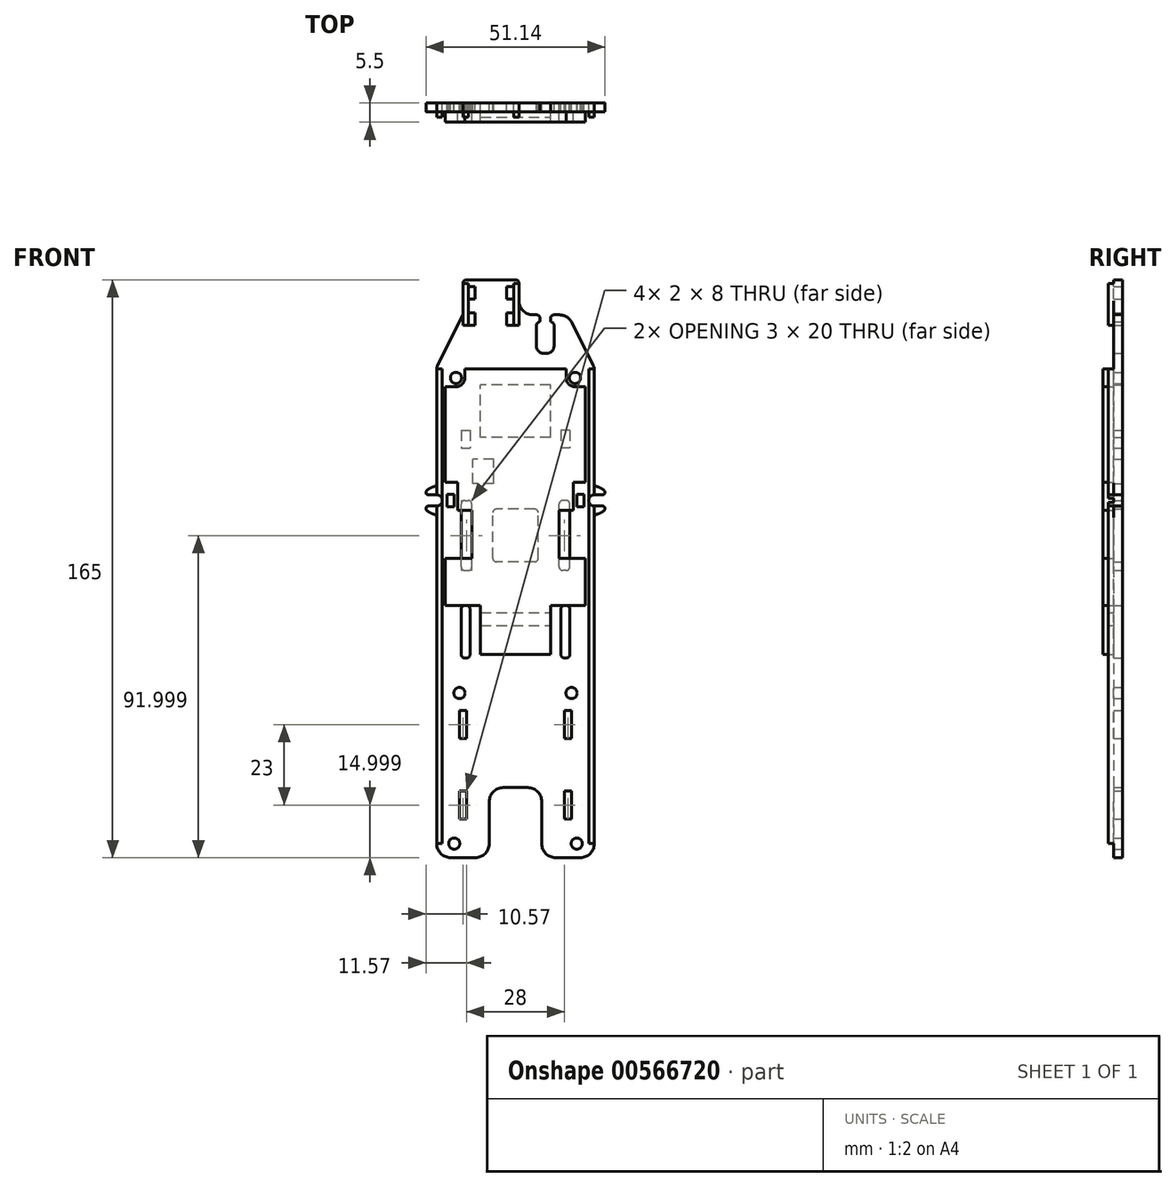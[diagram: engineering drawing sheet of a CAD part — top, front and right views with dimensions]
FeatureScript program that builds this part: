
annotation { "Feature Type Name" : "Feature", "Feature Type Description" : "" }
export const myFeature = defineFeature(function(context is Context, id is Id, definition is map)
    precondition{}
    {
        {
            var Q0;
            Q0=qCreatedBy(makeId("Front.planeOp"),FACE);
            var sketch = newSketch(context, id + "F0", { "sketchPlane" : qUnion([Q0])});
            skPoint(sketch, "E0", {"position": v(-17.5, -62.27) * mm});
            skPoint(sketch, "E1", {"position": v(-16, -19.27) * mm});
            skPoint(sketch, "E2", {"position": v(-17, 70.73) * mm});
            skPoint(sketch, "E3.MirrorP", {"position": v(17, 70.73) * mm});
            skPoint(sketch, "E4.MirrorP", {"position": v(16, -19.27) * mm});
            skPoint(sketch, "E5.MirrorP", {"position": v(17.5, -62.27) * mm});
            skLineSegment(sketch, "E6.bottom", {"start": v(-22.5, 73.73) * mm, "end": v(22.5, 73.73) * mm});
            skLineSegment(sketch, "E6.top", {"start": v(-18.5, -66.27) * mm, "end": v(-11.5, -66.27) * mm});
            skLineSegment(sketch, "E6.left", {"start": v(-22.5, 73.26) * mm, "end": v(-22.5, 40.63) * mm});
            skLineSegment(sketch, "E6.right", {"start": v(22.5, 73.26) * mm, "end": v(22.5, 40.63) * mm});
            skLineSegment(sketch, "E7.top", {"start": v(3.5, -46.27) * mm, "end": v(-3.5, -46.27) * mm});
            skLineSegment(sketch, "E7.left", {"start": v(7.5, -62.27) * mm, "end": v(7.5, -50.27) * mm});
            skLineSegment(sketch, "E7.right", {"start": v(-7.5, -62.27) * mm, "end": v(-7.5, -50.27) * mm});
            skPoint(sketch, "E7.middle", {"position": v(0, -56.27) * mm});
            skPoint(sketch, "E8.visualSharp", {"position": v(-22.5, -66.27) * mm});
            skArc(sketch, "E8.filletArc", {"start": v(-22.5, -62.27) * mm, "mid": v(-21.33, -65.1) * mm, "end": v(-18.5, -66.27) * mm});
            skPoint(sketch, "E9.visualSharp", {"position": v(22.5, -66.27) * mm});
            skArc(sketch, "E9.filletArc", {"start": v(18.5, -66.27) * mm, "mid": v(21.33, -65.1) * mm, "end": v(22.5, -62.27) * mm});
            skPoint(sketch, "E10.visualSharp", {"position": v(-7.5, -46.27) * mm});
            skArc(sketch, "E10.filletArc", {"start": v(-3.5, -46.27) * mm, "mid": v(-6.33, -47.44) * mm, "end": v(-7.5, -50.27) * mm});
            skPoint(sketch, "E11.visualSharp", {"position": v(7.5, -46.27) * mm});
            skArc(sketch, "E11.filletArc", {"start": v(7.5, -50.27) * mm, "mid": v(6.33, -47.44) * mm, "end": v(3.5, -46.27) * mm});
            skLineSegment(sketch, "E12.trimOffspring", {"start": v(11.5, -66.27) * mm, "end": v(18.5, -66.27) * mm});
            skPoint(sketch, "E13.visualSharp", {"position": v(-7.5, -66.27) * mm});
            skArc(sketch, "E13.filletArc", {"start": v(-11.5, -66.27) * mm, "mid": v(-8.67, -65.1) * mm, "end": v(-7.5, -62.27) * mm});
            skPoint(sketch, "E14.visualSharp", {"position": v(7.5, -66.27) * mm});
            skArc(sketch, "E14.filletArc", {"start": v(7.5, -62.27) * mm, "mid": v(8.67, -65.1) * mm, "end": v(11.5, -66.27) * mm});
            skLineSegment(sketch, "E15.bottom", {"start": v(-16, -47.27) * mm, "end": v(-14, -47.27) * mm});
            skLineSegment(sketch, "E15.top", {"start": v(-16, -55.27) * mm, "end": v(-14, -55.27) * mm});
            skLineSegment(sketch, "E15.left", {"start": v(-16, -47.27) * mm, "end": v(-16, -55.27) * mm});
            skLineSegment(sketch, "E15.right", {"start": v(-14, -47.27) * mm, "end": v(-14, -55.27) * mm});
            skLineSegment(sketch, "E16.MirrorCS", {"start": v(16, -47.27) * mm, "end": v(16, -55.27) * mm});
            skLineSegment(sketch, "E17.MirrorCS", {"start": v(14, -47.27) * mm, "end": v(14, -55.27) * mm});
            skLineSegment(sketch, "E18.MirrorCS", {"start": v(16, -47.27) * mm, "end": v(14, -47.27) * mm});
            skLineSegment(sketch, "E19.MirrorCS", {"start": v(16, -55.27) * mm, "end": v(14, -55.27) * mm});
            skLineSegment(sketch, "E20", {"start": v(-22.29, 74.15) * mm, "end": v(-15, 88.73) * mm});
            skLineSegment(sketch, "E21", {"start": v(5, 88.73) * mm, "end": v(6, 88.73) * mm});
            skLineSegment(sketch, "E22", {"start": v(16.1, 86.52) * mm, "end": v(22.29, 74.15) * mm});
            skLineSegment(sketch, "E23.top", {"start": v(-14, 98.73) * mm, "end": v(0, 98.73) * mm});
            skLineSegment(sketch, "E23.left", {"start": v(-15, 88.73) * mm, "end": v(-15, 97.73) * mm});
            skLineSegment(sketch, "E23.right", {"start": v(1, 92.73) * mm, "end": v(1, 97.73) * mm});
            skLineSegment(sketch, "E24.bottom", {"start": v(-13.5, 93.23) * mm, "end": v(-11.5, 93.23) * mm});
            skLineSegment(sketch, "E24.top", {"start": v(-13.5, 96.73) * mm, "end": v(-11.5, 96.73) * mm});
            skLineSegment(sketch, "E24.left", {"start": v(-13.5, 93.23) * mm, "end": v(-13.5, 96.73) * mm});
            skLineSegment(sketch, "E24.right", {"start": v(-11.5, 93.23) * mm, "end": v(-11.5, 96.73) * mm});
            skLineSegment(sketch, "E25", {"start": v(-7, 98.73) * mm, "end": v(-7, 82.75) * mm, "construction": true});
            skLineSegment(sketch, "E26.MirrorCS", {"start": v(-2.5, 93.23) * mm, "end": v(-2.5, 96.73) * mm});
            skLineSegment(sketch, "E27.MirrorCS", {"start": v(-0.5, 96.73) * mm, "end": v(-2.5, 96.73) * mm});
            skLineSegment(sketch, "E28.MirrorCS", {"start": v(-0.5, 93.23) * mm, "end": v(-0.5, 96.73) * mm});
            skLineSegment(sketch, "E29.MirrorCS", {"start": v(-0.5, 93.23) * mm, "end": v(-2.5, 93.23) * mm});
            skLineSegment(sketch, "E30", {"start": v(-15, 91.23) * mm, "end": v(1, 91.23) * mm, "construction": true});
            skLineSegment(sketch, "E31.MirrorCS", {"start": v(-13.5, 85.73) * mm, "end": v(-11.5, 85.73) * mm});
            skLineSegment(sketch, "E32.MirrorCS", {"start": v(-13.5, 89.23) * mm, "end": v(-13.5, 85.73) * mm});
            skLineSegment(sketch, "E33.MirrorCS", {"start": v(-13.5, 89.23) * mm, "end": v(-11.5, 89.23) * mm});
            skLineSegment(sketch, "E34.MirrorCS", {"start": v(-11.5, 89.23) * mm, "end": v(-11.5, 85.73) * mm});
            skLineSegment(sketch, "E35.MirrorCS", {"start": v(-2.5, 89.23) * mm, "end": v(-2.5, 85.73) * mm});
            skLineSegment(sketch, "E36.MirrorCS", {"start": v(-0.5, 85.73) * mm, "end": v(-2.5, 85.73) * mm});
            skLineSegment(sketch, "E37.MirrorCS", {"start": v(-0.5, 89.23) * mm, "end": v(-0.5, 85.73) * mm});
            skLineSegment(sketch, "E38.MirrorCS", {"start": v(-0.5, 89.23) * mm, "end": v(-2.5, 89.23) * mm});
            skPoint(sketch, "E39.visualSharp", {"position": v(1, 88.73) * mm});
            skArc(sketch, "E39.filletArc", {"start": v(1, 92.73) * mm, "mid": v(2.17, 89.9) * mm, "end": v(5, 88.73) * mm});
            skPoint(sketch, "E40.visualSharp", {"position": v(15, 88.73) * mm});
            skArc(sketch, "E40.filletArc", {"start": v(16.1, 86.52) * mm, "mid": v(14.63, 88.13) * mm, "end": v(12.53, 88.73) * mm});
            skPoint(sketch, "E41.visualSharp", {"position": v(1, 98.73) * mm});
            skArc(sketch, "E41.filletArc", {"start": v(1, 97.73) * mm, "mid": v(0.7, 98.44) * mm, "end": v(0, 98.73) * mm});
            skPoint(sketch, "E42.visualSharp", {"position": v(-15, 98.73) * mm});
            skArc(sketch, "E42.filletArc", {"start": v(-14, 98.73) * mm, "mid": v(-14.7, 98.44) * mm, "end": v(-15, 97.73) * mm});
            skPoint(sketch, "E43.visualSharp", {"position": v(22.5, 73.73) * mm});
            skArc(sketch, "E43.filletArc", {"start": v(22.5, 73.26) * mm, "mid": v(22.45, 73.72) * mm, "end": v(22.29, 74.15) * mm});
            skPoint(sketch, "E44.visualSharp", {"position": v(-22.5, 73.73) * mm});
            skArc(sketch, "E44.filletArc", {"start": v(-22.29, 74.15) * mm, "mid": v(-22.45, 73.72) * mm, "end": v(-22.5, 73.26) * mm});
            skLineSegment(sketch, "E45.left", {"start": v(7, 87.73) * mm, "end": v(7, 86.73) * mm});
            skLineSegment(sketch, "E45.right", {"start": v(10, 87.73) * mm, "end": v(10, 86.73) * mm});
            skLineSegment(sketch, "E46.trimOffspring", {"start": v(11, 88.73) * mm, "end": v(12.53, 88.73) * mm});
            skPoint(sketch, "E47.visualSharp", {"position": v(10, 88.73) * mm});
            skArc(sketch, "E47.filletArc", {"start": v(11, 88.73) * mm, "mid": v(10.3, 88.44) * mm, "end": v(10, 87.73) * mm});
            skPoint(sketch, "E48.visualSharp", {"position": v(7, 88.73) * mm});
            skArc(sketch, "E48.filletArc", {"start": v(7, 87.73) * mm, "mid": v(6.7, 88.44) * mm, "end": v(6, 88.73) * mm});
            skPoint(sketch, "E49.visualSharp", {"position": v(7, 76.73) * mm});
            skPoint(sketch, "E50.visualSharp", {"position": v(10, 76.73) * mm});
            skLineSegment(sketch, "E51", {"start": v(-22.5, -39.77) * mm, "end": v(22.5, -39.77) * mm, "construction": true});
            skLineSegment(sketch, "E52.MirrorCS", {"start": v(16, -32.27) * mm, "end": v(16, -24.27) * mm});
            skLineSegment(sketch, "E53.MirrorCS", {"start": v(14, -32.27) * mm, "end": v(14, -24.27) * mm});
            skLineSegment(sketch, "E54.MirrorCS", {"start": v(16, -32.27) * mm, "end": v(14, -32.27) * mm});
            skLineSegment(sketch, "E55.MirrorCS", {"start": v(16, -24.27) * mm, "end": v(14, -24.27) * mm});
            skLineSegment(sketch, "E56.MirrorCS", {"start": v(-14, -32.27) * mm, "end": v(-14, -24.27) * mm});
            skLineSegment(sketch, "E57.MirrorCS", {"start": v(-16, -32.27) * mm, "end": v(-14, -32.27) * mm});
            skLineSegment(sketch, "E58.MirrorCS", {"start": v(-16, -32.27) * mm, "end": v(-16, -24.27) * mm});
            skLineSegment(sketch, "E59.MirrorCS", {"start": v(-16, -24.27) * mm, "end": v(-14, -24.27) * mm});
            skLineSegment(sketch, "E60.bottom", {"start": v(-14.5, -9.27) * mm, "end": v(-14, -9.27) * mm});
            skLineSegment(sketch, "E60.top", {"start": v(-14.5, 5.73) * mm, "end": v(-14, 5.73) * mm});
            skLineSegment(sketch, "E60.left", {"start": v(-15.5, -8.27) * mm, "end": v(-15.5, 4.73) * mm});
            skLineSegment(sketch, "E60.right", {"start": v(-13, -8.27) * mm, "end": v(-13, 4.73) * mm});
            skLineSegment(sketch, "E61.MirrorCS", {"start": v(13, -8.27) * mm, "end": v(13, 4.73) * mm});
            skLineSegment(sketch, "E62.MirrorCS", {"start": v(14.5, 5.73) * mm, "end": v(14, 5.73) * mm});
            skLineSegment(sketch, "E63.MirrorCS", {"start": v(15.5, -8.27) * mm, "end": v(15.5, 4.73) * mm});
            skLineSegment(sketch, "E64.MirrorCS", {"start": v(14.5, -9.27) * mm, "end": v(14, -9.27) * mm});
            skLineSegment(sketch, "E65.bottom", {"start": v(-14.5, 15.73) * mm, "end": v(-13.5, 15.73) * mm});
            skLineSegment(sketch, "E65.top", {"start": v(-14.5, 35.73) * mm, "end": v(-13.5, 35.73) * mm});
            skLineSegment(sketch, "E65.left", {"start": v(-15.5, 16.73) * mm, "end": v(-15.5, 34.73) * mm});
            skLineSegment(sketch, "E65.right", {"start": v(-12.5, 16.73) * mm, "end": v(-12.5, 34.73) * mm});
            skLineSegment(sketch, "E66.MirrorCS", {"start": v(14.5, 15.73) * mm, "end": v(13.5, 15.73) * mm});
            skLineSegment(sketch, "E67.MirrorCS", {"start": v(12.5, 16.73) * mm, "end": v(12.5, 34.73) * mm});
            skLineSegment(sketch, "E68.MirrorCS", {"start": v(14.5, 35.73) * mm, "end": v(13.5, 35.73) * mm});
            skLineSegment(sketch, "E69.MirrorCS", {"start": v(15.5, 16.73) * mm, "end": v(15.5, 34.73) * mm});
            skLineSegment(sketch, "E70.bottom", {"start": v(5.5, 18.23) * mm, "end": v(-5.5, 18.23) * mm});
            skLineSegment(sketch, "E70.top", {"start": v(5.5, 33.23) * mm, "end": v(-5.5, 33.23) * mm});
            skLineSegment(sketch, "E70.left", {"start": v(6.5, 19.23) * mm, "end": v(6.5, 32.23) * mm});
            skLineSegment(sketch, "E70.right", {"start": v(-6.5, 19.23) * mm, "end": v(-6.5, 32.23) * mm});
            skPoint(sketch, "E70.middle", {"position": v(0, 25.73) * mm});
            skPoint(sketch, "E70.middle.positionSnap0", {"position": v(-12.5, 25.73) * mm});
            skPoint(sketch, "E70.centerSnap0", {"position": v(-12.5, 25.73) * mm});
            skPoint(sketch, "E71.visualSharp", {"position": v(-6.5, 33.23) * mm});
            skArc(sketch, "E71.filletArc", {"start": v(-5.5, 33.23) * mm, "mid": v(-6.2, 32.94) * mm, "end": v(-6.5, 32.23) * mm});
            skPoint(sketch, "E72.visualSharp", {"position": v(6.5, 33.23) * mm});
            skArc(sketch, "E72.filletArc", {"start": v(6.5, 32.23) * mm, "mid": v(6.2, 32.94) * mm, "end": v(5.5, 33.23) * mm});
            skPoint(sketch, "E73.visualSharp", {"position": v(6.5, 18.23) * mm});
            skArc(sketch, "E73.filletArc", {"start": v(5.5, 18.23) * mm, "mid": v(6.2, 18.52) * mm, "end": v(6.5, 19.23) * mm});
            skPoint(sketch, "E74.visualSharp", {"position": v(-6.5, 18.23) * mm});
            skArc(sketch, "E74.filletArc", {"start": v(-6.5, 19.23) * mm, "mid": v(-6.2, 18.52) * mm, "end": v(-5.5, 18.23) * mm});
            skPoint(sketch, "E75.visualSharp", {"position": v(-15.5, 15.73) * mm});
            skArc(sketch, "E75.filletArc", {"start": v(-15.5, 16.73) * mm, "mid": v(-15.2, 16.02) * mm, "end": v(-14.5, 15.73) * mm});
            skPoint(sketch, "E76.visualSharp", {"position": v(-15.5, 35.73) * mm});
            skArc(sketch, "E76.filletArc", {"start": v(-14.5, 35.73) * mm, "mid": v(-15.2, 35.44) * mm, "end": v(-15.5, 34.73) * mm});
            skPoint(sketch, "E77.visualSharp", {"position": v(-12.5, 15.73) * mm});
            skArc(sketch, "E77.filletArc", {"start": v(-13.5, 15.73) * mm, "mid": v(-12.8, 16.02) * mm, "end": v(-12.5, 16.73) * mm});
            skPoint(sketch, "E78.visualSharp", {"position": v(-12.5, 35.73) * mm});
            skArc(sketch, "E78.filletArc", {"start": v(-12.5, 34.73) * mm, "mid": v(-12.8, 35.44) * mm, "end": v(-13.5, 35.73) * mm});
            skPoint(sketch, "E79.visualSharp", {"position": v(12.5, 35.73) * mm});
            skArc(sketch, "E79.filletArc", {"start": v(13.5, 35.73) * mm, "mid": v(12.8, 35.44) * mm, "end": v(12.5, 34.73) * mm});
            skPoint(sketch, "E80.visualSharp", {"position": v(15.5, 35.73) * mm});
            skArc(sketch, "E80.filletArc", {"start": v(15.5, 34.73) * mm, "mid": v(15.2, 35.44) * mm, "end": v(14.5, 35.73) * mm});
            skPoint(sketch, "E81.visualSharp", {"position": v(12.5, 15.73) * mm});
            skArc(sketch, "E81.filletArc", {"start": v(12.5, 16.73) * mm, "mid": v(12.8, 16.02) * mm, "end": v(13.5, 15.73) * mm});
            skPoint(sketch, "E82.visualSharp", {"position": v(15.5, 15.73) * mm});
            skArc(sketch, "E82.filletArc", {"start": v(14.5, 15.73) * mm, "mid": v(15.2, 16.02) * mm, "end": v(15.5, 16.73) * mm});
            skPoint(sketch, "E83.visualSharp", {"position": v(13, 5.73) * mm});
            skArc(sketch, "E83.filletArc", {"start": v(14, 5.73) * mm, "mid": v(13.3, 5.44) * mm, "end": v(13, 4.73) * mm});
            skPoint(sketch, "E84.visualSharp", {"position": v(15.5, 5.73) * mm});
            skArc(sketch, "E84.filletArc", {"start": v(15.5, 4.73) * mm, "mid": v(15.2, 5.44) * mm, "end": v(14.5, 5.73) * mm});
            skPoint(sketch, "E85.visualSharp", {"position": v(13, -9.27) * mm});
            skArc(sketch, "E85.filletArc", {"start": v(13, -8.27) * mm, "mid": v(13.3, -8.98) * mm, "end": v(14, -9.27) * mm});
            skPoint(sketch, "E86.visualSharp", {"position": v(15.5, -9.27) * mm});
            skArc(sketch, "E86.filletArc", {"start": v(14.5, -9.27) * mm, "mid": v(15.2, -8.98) * mm, "end": v(15.5, -8.27) * mm});
            skPoint(sketch, "E87.visualSharp", {"position": v(-15.5, -9.27) * mm});
            skArc(sketch, "E87.filletArc", {"start": v(-15.5, -8.27) * mm, "mid": v(-15.2, -8.98) * mm, "end": v(-14.5, -9.27) * mm});
            skPoint(sketch, "E88.visualSharp", {"position": v(-15.5, 5.73) * mm});
            skArc(sketch, "E88.filletArc", {"start": v(-14.5, 5.73) * mm, "mid": v(-15.2, 5.44) * mm, "end": v(-15.5, 4.73) * mm});
            skPoint(sketch, "E89.visualSharp", {"position": v(-13, 5.73) * mm});
            skArc(sketch, "E89.filletArc", {"start": v(-13, 4.73) * mm, "mid": v(-13.3, 5.44) * mm, "end": v(-14, 5.73) * mm});
            skPoint(sketch, "E90.visualSharp", {"position": v(-13, -9.27) * mm});
            skArc(sketch, "E90.filletArc", {"start": v(-14, -9.27) * mm, "mid": v(-13.3, -8.98) * mm, "end": v(-13, -8.27) * mm});
            skLineSegment(sketch, "E91.bottom", {"start": v(-15.5, 55.73) * mm, "end": v(-13, 55.73) * mm});
            skLineSegment(sketch, "E91.top", {"start": v(-15.5, 50.73) * mm, "end": v(-13, 50.73) * mm});
            skLineSegment(sketch, "E91.left", {"start": v(-15.5, 55.73) * mm, "end": v(-15.5, 50.73) * mm});
            skLineSegment(sketch, "E91.right", {"start": v(-13, 55.73) * mm, "end": v(-13, 50.73) * mm});
            skLineSegment(sketch, "E92.MirrorCS", {"start": v(15.5, 50.73) * mm, "end": v(13, 50.73) * mm});
            skLineSegment(sketch, "E93.MirrorCS", {"start": v(15.5, 55.73) * mm, "end": v(13, 55.73) * mm});
            skLineSegment(sketch, "E94.MirrorCS", {"start": v(13, 55.73) * mm, "end": v(13, 50.73) * mm});
            skLineSegment(sketch, "E95.MirrorCS", {"start": v(15.5, 55.73) * mm, "end": v(15.5, 50.73) * mm});
            skLineSegment(sketch, "E96.bottom", {"start": v(10, 53.73) * mm, "end": v(-10, 53.73) * mm});
            skLineSegment(sketch, "E96.top", {"start": v(10, 68.73) * mm, "end": v(-10, 68.73) * mm});
            skLineSegment(sketch, "E96.left", {"start": v(10, 53.73) * mm, "end": v(10, 68.73) * mm});
            skLineSegment(sketch, "E96.right", {"start": v(-10, 53.73) * mm, "end": v(-10, 68.73) * mm});
            skPoint(sketch, "E96.middle", {"position": v(0, 61.23) * mm});
            skLineSegment(sketch, "E97.bottom", {"start": v(-6.17, 40.53) * mm, "end": v(-12.17, 40.53) * mm});
            skLineSegment(sketch, "E97.top", {"start": v(-6.17, 47.53) * mm, "end": v(-12.17, 47.53) * mm});
            skLineSegment(sketch, "E97.left", {"start": v(-6.17, 40.53) * mm, "end": v(-6.17, 47.53) * mm});
            skLineSegment(sketch, "E97.right", {"start": v(-12.17, 40.53) * mm, "end": v(-12.17, 47.53) * mm});
            skPoint(sketch, "E97.middle", {"position": v(-9.17, 44.03) * mm});
            skLineSegment(sketch, "E98.bottom", {"start": v(9, 77.73) * mm, "end": v(8, 77.73) * mm});
            skLineSegment(sketch, "E98.top", {"start": v(10, 86.73) * mm, "end": v(10, 86.73) * mm});
            skLineSegment(sketch, "E98.left", {"start": v(11, 79.73) * mm, "end": v(11, 85.73) * mm});
            skLineSegment(sketch, "E98.right", {"start": v(6, 79.73) * mm, "end": v(6, 85.73) * mm});
            skPoint(sketch, "E98.middle", {"position": v(8.5, 82.23) * mm});
            skPoint(sketch, "E98.middle.positionSnap0", {"position": v(8.5, 76.73) * mm});
            skPoint(sketch, "E98.centerSnap0", {"position": v(8.5, 76.73) * mm});
            skPoint(sketch, "E99.orphan", {"position": v(8, 76.73) * mm});
            skPoint(sketch, "E45.top.end.orphan", {"position": v(9, 76.73) * mm});
            skLineSegment(sketch, "E100.trimOffspring", {"start": v(7, 86.73) * mm, "end": v(7, 86.73) * mm});
            skPoint(sketch, "E101.visualSharp", {"position": v(6, 77.73) * mm});
            skArc(sketch, "E101.filletArc", {"start": v(6, 79.73) * mm, "mid": v(6.59, 78.31) * mm, "end": v(8, 77.73) * mm});
            skPoint(sketch, "E102.visualSharp", {"position": v(11, 77.73) * mm});
            skArc(sketch, "E102.filletArc", {"start": v(9, 77.73) * mm, "mid": v(10.41, 78.31) * mm, "end": v(11, 79.73) * mm});
            skPoint(sketch, "E103.visualSharp", {"position": v(6, 86.73) * mm});
            skArc(sketch, "E103.filletArc", {"start": v(7, 86.73) * mm, "mid": v(6.3, 86.44) * mm, "end": v(6, 85.73) * mm});
            skPoint(sketch, "E104.visualSharp", {"position": v(11, 86.73) * mm});
            skArc(sketch, "E104.filletArc", {"start": v(11, 85.73) * mm, "mid": v(10.7, 86.44) * mm, "end": v(10, 86.73) * mm});
            skArc(sketch, "E105", {"start": v(-23.3, 39.65) * mm, "mid": v(-24.42, 39.24) * mm, "end": v(-25.37, 38.52) * mm});
            skArc(sketch, "E106", {"start": v(-22.5, 34.13) * mm, "mid": v(-20.9, 35.73) * mm, "end": v(-22.5, 37.33) * mm});
            skLineSegment(sketch, "E107", {"start": v(-22.5, 37.33) * mm, "end": v(-24.87, 37.33) * mm});
            skLineSegment(sketch, "E108", {"start": v(-22.5, 34.13) * mm, "end": v(-24.87, 34.13) * mm});
            skArc(sketch, "E109.trimOffspring", {"start": v(-25.37, 32.94) * mm, "mid": v(-24.42, 32.22) * mm, "end": v(-23.3, 31.8) * mm});
            skPoint(sketch, "E110.visualSharp", {"position": v(-26.17, 37.33) * mm});
            skArc(sketch, "E110.filletArc", {"start": v(-25.37, 38.52) * mm, "mid": v(-25.51, 37.76) * mm, "end": v(-24.87, 37.33) * mm});
            skPoint(sketch, "E111.visualSharp", {"position": v(-26.17, 34.13) * mm});
            skArc(sketch, "E111.filletArc", {"start": v(-24.87, 34.13) * mm, "mid": v(-25.51, 33.7) * mm, "end": v(-25.37, 32.94) * mm});
            skLineSegment(sketch, "E112.trimOffspring", {"start": v(-22.5, 30.83) * mm, "end": v(-22.5, -62.27) * mm});
            skPoint(sketch, "E113.visualSharp", {"position": v(-22.5, 39.73) * mm});
            skArc(sketch, "E113.filletArc", {"start": v(-23.3, 39.65) * mm, "mid": v(-22.73, 40) * mm, "end": v(-22.5, 40.63) * mm});
            skPoint(sketch, "E114.visualSharp", {"position": v(-22.5, 31.73) * mm});
            skArc(sketch, "E114.filletArc", {"start": v(-22.5, 30.83) * mm, "mid": v(-22.73, 31.46) * mm, "end": v(-23.3, 31.8) * mm});
            skLineSegment(sketch, "E115.bottom", {"start": v(-19.5, 37.48) * mm, "end": v(-17.5, 37.48) * mm});
            skLineSegment(sketch, "E115.top", {"start": v(-19.5, 33.98) * mm, "end": v(-17.5, 33.98) * mm});
            skLineSegment(sketch, "E115.left", {"start": v(-19.5, 37.48) * mm, "end": v(-19.5, 33.98) * mm});
            skLineSegment(sketch, "E115.right", {"start": v(-17.5, 37.48) * mm, "end": v(-17.5, 33.98) * mm});
            skPoint(sketch, "E115.middle", {"position": v(-18.5, 35.73) * mm});
            skLineSegment(sketch, "E116.MirrorCS", {"start": v(19.5, 37.48) * mm, "end": v(17.5, 37.48) * mm});
            skLineSegment(sketch, "E117.MirrorCS", {"start": v(17.5, 37.48) * mm, "end": v(17.5, 33.98) * mm});
            skLineSegment(sketch, "E118.MirrorCS", {"start": v(19.5, 33.98) * mm, "end": v(17.5, 33.98) * mm});
            skLineSegment(sketch, "E119.MirrorCS", {"start": v(19.5, 37.48) * mm, "end": v(19.5, 33.98) * mm});
            skArc(sketch, "E120.MirrorCS", {"start": v(25.37, 32.94) * mm, "mid": v(24.42, 32.22) * mm, "end": v(23.3, 31.8) * mm});
            skPoint(sketch, "E121.MirrorP", {"position": v(22.5, 31.73) * mm});
            skPoint(sketch, "E122.MirrorP", {"position": v(26.17, 34.13) * mm});
            skArc(sketch, "E123.MirrorCS", {"start": v(24.87, 34.13) * mm, "mid": v(25.51, 33.7) * mm, "end": v(25.37, 32.94) * mm});
            skPoint(sketch, "E124.MirrorP", {"position": v(26.17, 37.33) * mm});
            skArc(sketch, "E125.MirrorCS", {"start": v(25.37, 38.52) * mm, "mid": v(25.51, 37.76) * mm, "end": v(24.87, 37.33) * mm});
            skPoint(sketch, "E126.MirrorP", {"position": v(22.5, 39.73) * mm});
            skArc(sketch, "E127.MirrorCS", {"start": v(23.3, 39.65) * mm, "mid": v(24.42, 39.24) * mm, "end": v(25.37, 38.52) * mm});
            skArc(sketch, "E128.MirrorCS", {"start": v(22.5, 34.13) * mm, "mid": v(20.9, 35.73) * mm, "end": v(22.5, 37.33) * mm});
            skLineSegment(sketch, "E129.MirrorCS", {"start": v(22.5, 37.33) * mm, "end": v(24.87, 37.33) * mm});
            skLineSegment(sketch, "E130.MirrorCS", {"start": v(22.5, 34.13) * mm, "end": v(24.87, 34.13) * mm});
            skArc(sketch, "E131.MirrorCS", {"start": v(23.3, 39.65) * mm, "mid": v(22.73, 40) * mm, "end": v(22.5, 40.63) * mm});
            skArc(sketch, "E132.MirrorCS", {"start": v(22.5, 30.83) * mm, "mid": v(22.73, 31.46) * mm, "end": v(23.3, 31.8) * mm});
            skLineSegment(sketch, "E133.trimOffspring", {"start": v(22.5, 30.83) * mm, "end": v(22.5, -62.27) * mm});
            skSolve(sketch);
        }
        {
            var Q0;
            Q0=makeQuery(id+"F0.imprint","IMPRINT",FACE,{"disambiguationData":[TD([[makeQuery(id+"F0.imprint","IMPRINT",EDGE,{"derivedFrom":sQuery(id+"F0.wireOp",EDGE,"E6.top")}),1.0]])]});
            var Q1;
            {var subQ1=sQuery(id+"F0.wireOp",EDGE,"E20");Q1=makeQuery(id+"F0.imprint","IMPRINT",FACE,{"disambiguationData":[TD([[makeQuery(id+"F0.imprint","IMPRINT",EDGE,{"derivedFrom":subQ1}),-1.0]])]});}
            extrude(context, id + "F1", {"entities" : qUnion([Q0, Q1]), "depth" : 2.5 * mm, "offsetDistance" : 25 * mm});
        }
        {
            var Q0;
            Q0=sQuery(id+"F0.wireOp",VERTEX,"E2");
            var Q1;
            Q1=sQuery(id+"F0.wireOp",VERTEX,"E3.MirrorP");
            var Q2;
            Q2=sQuery(id+"F0.wireOp",VERTEX,"E1");
            var Q3;
            Q3=sQuery(id+"F0.wireOp",VERTEX,"E4.MirrorP");
            var Q4;
            Q4=sQuery(id+"F0.wireOp",VERTEX,"E0");
            var Q5;
            Q5=sQuery(id+"F0.wireOp",VERTEX,"E5.MirrorP");
            var Q6;
            Q6=makeQuery(id+"F1.opExtrude","SWEPT_BODY",BODY,{"disambiguationData":[OSD([sQuery(id+"F0.wireOp",EDGE,"E6.top"),sQuery(id+"F0.wireOp",EDGE,"E6.left"),sQuery(id+"F0.wireOp",EDGE,"E6.right"),sQuery(id+"F0.wireOp",EDGE,"E7.top"),sQuery(id+"F0.wireOp",EDGE,"E7.left"),sQuery(id+"F0.wireOp",EDGE,"E7.right"),sQuery(id+"F0.wireOp",EDGE,"E8.filletArc"),sQuery(id+"F0.wireOp",EDGE,"E9.filletArc"),sQuery(id+"F0.wireOp",EDGE,"E10.filletArc"),sQuery(id+"F0.wireOp",EDGE,"E11.filletArc"),sQuery(id+"F0.wireOp",EDGE,"E12.trimOffspring"),sQuery(id+"F0.wireOp",EDGE,"E13.filletArc"),sQuery(id+"F0.wireOp",EDGE,"E14.filletArc"),sQuery(id+"F0.wireOp",EDGE,"E15.bottom"),sQuery(id+"F0.wireOp",EDGE,"E15.top"),sQuery(id+"F0.wireOp",EDGE,"E15.left"),sQuery(id+"F0.wireOp",EDGE,"E15.right"),sQuery(id+"F0.wireOp",EDGE,"E16.MirrorCS"),sQuery(id+"F0.wireOp",EDGE,"E17.MirrorCS"),sQuery(id+"F0.wireOp",EDGE,"E18.MirrorCS"),sQuery(id+"F0.wireOp",EDGE,"E19.MirrorCS"),sQuery(id+"F0.wireOp",EDGE,"E20"),sQuery(id+"F0.wireOp",EDGE,"E21"),sQuery(id+"F0.wireOp",EDGE,"E22"),sQuery(id+"F0.wireOp",EDGE,"E23.top"),sQuery(id+"F0.wireOp",EDGE,"E23.left"),sQuery(id+"F0.wireOp",EDGE,"E23.right"),sQuery(id+"F0.wireOp",EDGE,"E24.bottom"),sQuery(id+"F0.wireOp",EDGE,"E24.top"),sQuery(id+"F0.wireOp",EDGE,"E24.left"),sQuery(id+"F0.wireOp",EDGE,"E24.right"),sQuery(id+"F0.wireOp",EDGE,"E26.MirrorCS"),sQuery(id+"F0.wireOp",EDGE,"E27.MirrorCS"),sQuery(id+"F0.wireOp",EDGE,"E28.MirrorCS"),sQuery(id+"F0.wireOp",EDGE,"E29.MirrorCS"),sQuery(id+"F0.wireOp",EDGE,"E31.MirrorCS"),sQuery(id+"F0.wireOp",EDGE,"E32.MirrorCS"),sQuery(id+"F0.wireOp",EDGE,"E33.MirrorCS"),sQuery(id+"F0.wireOp",EDGE,"E34.MirrorCS"),sQuery(id+"F0.wireOp",EDGE,"E35.MirrorCS"),sQuery(id+"F0.wireOp",EDGE,"E36.MirrorCS"),sQuery(id+"F0.wireOp",EDGE,"E37.MirrorCS"),sQuery(id+"F0.wireOp",EDGE,"E38.MirrorCS"),sQuery(id+"F0.wireOp",EDGE,"E39.filletArc"),sQuery(id+"F0.wireOp",EDGE,"E40.filletArc"),sQuery(id+"F0.wireOp",EDGE,"E41.filletArc"),sQuery(id+"F0.wireOp",EDGE,"E42.filletArc"),sQuery(id+"F0.wireOp",EDGE,"E43.filletArc"),sQuery(id+"F0.wireOp",EDGE,"E44.filletArc"),sQuery(id+"F0.wireOp",EDGE,"E45.top"),sQuery(id+"F0.wireOp",EDGE,"E45.left"),sQuery(id+"F0.wireOp",EDGE,"E45.right"),sQuery(id+"F0.wireOp",EDGE,"E46.trimOffspring"),sQuery(id+"F0.wireOp",EDGE,"E47.filletArc"),sQuery(id+"F0.wireOp",EDGE,"E48.filletArc"),sQuery(id+"F0.wireOp",EDGE,"E49.filletArc"),sQuery(id+"F0.wireOp",EDGE,"E50.filletArc"),sQuery(id+"F0.wireOp",EDGE,"E52.MirrorCS"),sQuery(id+"F0.wireOp",EDGE,"E53.MirrorCS"),sQuery(id+"F0.wireOp",EDGE,"E54.MirrorCS"),sQuery(id+"F0.wireOp",EDGE,"E55.MirrorCS"),sQuery(id+"F0.wireOp",EDGE,"E56.MirrorCS"),sQuery(id+"F0.wireOp",EDGE,"E57.MirrorCS"),sQuery(id+"F0.wireOp",EDGE,"E58.MirrorCS"),sQuery(id+"F0.wireOp",EDGE,"E59.MirrorCS"),sQuery(id+"F0.wireOp",EDGE,"E60.bottom"),sQuery(id+"F0.wireOp",EDGE,"E60.top"),sQuery(id+"F0.wireOp",EDGE,"E60.left"),sQuery(id+"F0.wireOp",EDGE,"E60.right"),sQuery(id+"F0.wireOp",EDGE,"E61.MirrorCS"),sQuery(id+"F0.wireOp",EDGE,"E62.MirrorCS"),sQuery(id+"F0.wireOp",EDGE,"E63.MirrorCS"),sQuery(id+"F0.wireOp",EDGE,"E64.MirrorCS"),sQuery(id+"F0.wireOp",EDGE,"E65.bottom"),sQuery(id+"F0.wireOp",EDGE,"E65.top"),sQuery(id+"F0.wireOp",EDGE,"E65.left"),sQuery(id+"F0.wireOp",EDGE,"E65.right"),sQuery(id+"F0.wireOp",EDGE,"E66.MirrorCS"),sQuery(id+"F0.wireOp",EDGE,"E67.MirrorCS"),sQuery(id+"F0.wireOp",EDGE,"E68.MirrorCS"),sQuery(id+"F0.wireOp",EDGE,"E69.MirrorCS"),sQuery(id+"F0.wireOp",EDGE,"E70.bottom"),sQuery(id+"F0.wireOp",EDGE,"E70.top"),sQuery(id+"F0.wireOp",EDGE,"E70.left"),sQuery(id+"F0.wireOp",EDGE,"E70.right"),sQuery(id+"F0.wireOp",EDGE,"E71.filletArc"),sQuery(id+"F0.wireOp",EDGE,"E72.filletArc"),sQuery(id+"F0.wireOp",EDGE,"E73.filletArc"),sQuery(id+"F0.wireOp",EDGE,"E74.filletArc"),sQuery(id+"F0.wireOp",EDGE,"E75.filletArc"),sQuery(id+"F0.wireOp",EDGE,"E76.filletArc"),sQuery(id+"F0.wireOp",EDGE,"E77.filletArc"),sQuery(id+"F0.wireOp",EDGE,"E78.filletArc"),sQuery(id+"F0.wireOp",EDGE,"E79.filletArc"),sQuery(id+"F0.wireOp",EDGE,"E80.filletArc"),sQuery(id+"F0.wireOp",EDGE,"E81.filletArc"),sQuery(id+"F0.wireOp",EDGE,"E82.filletArc"),sQuery(id+"F0.wireOp",EDGE,"E83.filletArc"),sQuery(id+"F0.wireOp",EDGE,"E84.filletArc"),sQuery(id+"F0.wireOp",EDGE,"E85.filletArc"),sQuery(id+"F0.wireOp",EDGE,"E86.filletArc"),sQuery(id+"F0.wireOp",EDGE,"E87.filletArc"),sQuery(id+"F0.wireOp",EDGE,"E88.filletArc"),sQuery(id+"F0.wireOp",EDGE,"E89.filletArc"),sQuery(id+"F0.wireOp",EDGE,"E90.filletArc"),sQuery(id+"F0.wireOp",EDGE,"E91.bottom"),sQuery(id+"F0.wireOp",EDGE,"E91.top"),sQuery(id+"F0.wireOp",EDGE,"E91.left"),sQuery(id+"F0.wireOp",EDGE,"E91.right"),sQuery(id+"F0.wireOp",EDGE,"E92.MirrorCS"),sQuery(id+"F0.wireOp",EDGE,"E93.MirrorCS"),sQuery(id+"F0.wireOp",EDGE,"E94.MirrorCS"),sQuery(id+"F0.wireOp",EDGE,"E95.MirrorCS"),sQuery(id+"F0.wireOp",EDGE,"E96.bottom"),sQuery(id+"F0.wireOp",EDGE,"E96.top"),sQuery(id+"F0.wireOp",EDGE,"E96.left"),sQuery(id+"F0.wireOp",EDGE,"E96.right"),sQuery(id+"F0.wireOp",EDGE,"E97.bottom"),sQuery(id+"F0.wireOp",EDGE,"E97.top"),sQuery(id+"F0.wireOp",EDGE,"E97.left"),sQuery(id+"F0.wireOp",EDGE,"E97.right")])]});
            hole(context, id + "F2", {"style" : HoleStyle.SIMPLE, "endStyle" : HoleEndStyle.THROUGH, "oppositeDirection" : true, "holeDiameter" : 3.2 * mm, "isTappedThrough" : true, "tappedDepth" : 12 * mm, "tapClearance" : 3, "locations" : qUnion([Q0, Q1, Q2, Q3, Q4, Q5]), "scope" : qUnion([Q6])});
        }
        {
            var Q0;
            Q0=makeQuery(id+"F1.opExtrude","CAP_FACE",FACE,{"disambiguationData":[OSD([sQuery(id+"F0.wireOp",EDGE,"E6.top"),sQuery(id+"F0.wireOp",EDGE,"E6.left"),sQuery(id+"F0.wireOp",EDGE,"E6.right"),sQuery(id+"F0.wireOp",EDGE,"E7.top"),sQuery(id+"F0.wireOp",EDGE,"E7.left"),sQuery(id+"F0.wireOp",EDGE,"E7.right"),sQuery(id+"F0.wireOp",EDGE,"E8.filletArc"),sQuery(id+"F0.wireOp",EDGE,"E9.filletArc"),sQuery(id+"F0.wireOp",EDGE,"E10.filletArc"),sQuery(id+"F0.wireOp",EDGE,"E11.filletArc"),sQuery(id+"F0.wireOp",EDGE,"E12.trimOffspring"),sQuery(id+"F0.wireOp",EDGE,"E13.filletArc"),sQuery(id+"F0.wireOp",EDGE,"E14.filletArc"),sQuery(id+"F0.wireOp",EDGE,"E15.bottom"),sQuery(id+"F0.wireOp",EDGE,"E15.top"),sQuery(id+"F0.wireOp",EDGE,"E15.left"),sQuery(id+"F0.wireOp",EDGE,"E15.right"),sQuery(id+"F0.wireOp",EDGE,"E16.MirrorCS"),sQuery(id+"F0.wireOp",EDGE,"E17.MirrorCS"),sQuery(id+"F0.wireOp",EDGE,"E18.MirrorCS"),sQuery(id+"F0.wireOp",EDGE,"E19.MirrorCS"),sQuery(id+"F0.wireOp",EDGE,"E20"),sQuery(id+"F0.wireOp",EDGE,"E21"),sQuery(id+"F0.wireOp",EDGE,"E22"),sQuery(id+"F0.wireOp",EDGE,"E23.top"),sQuery(id+"F0.wireOp",EDGE,"E23.left"),sQuery(id+"F0.wireOp",EDGE,"E23.right"),sQuery(id+"F0.wireOp",EDGE,"E24.bottom"),sQuery(id+"F0.wireOp",EDGE,"E24.top"),sQuery(id+"F0.wireOp",EDGE,"E24.left"),sQuery(id+"F0.wireOp",EDGE,"E24.right"),sQuery(id+"F0.wireOp",EDGE,"E26.MirrorCS"),sQuery(id+"F0.wireOp",EDGE,"E27.MirrorCS"),sQuery(id+"F0.wireOp",EDGE,"E28.MirrorCS"),sQuery(id+"F0.wireOp",EDGE,"E29.MirrorCS"),sQuery(id+"F0.wireOp",EDGE,"E31.MirrorCS"),sQuery(id+"F0.wireOp",EDGE,"E32.MirrorCS"),sQuery(id+"F0.wireOp",EDGE,"E33.MirrorCS"),sQuery(id+"F0.wireOp",EDGE,"E34.MirrorCS"),sQuery(id+"F0.wireOp",EDGE,"E35.MirrorCS"),sQuery(id+"F0.wireOp",EDGE,"E36.MirrorCS"),sQuery(id+"F0.wireOp",EDGE,"E37.MirrorCS"),sQuery(id+"F0.wireOp",EDGE,"E38.MirrorCS"),sQuery(id+"F0.wireOp",EDGE,"E39.filletArc"),sQuery(id+"F0.wireOp",EDGE,"E40.filletArc"),sQuery(id+"F0.wireOp",EDGE,"E41.filletArc"),sQuery(id+"F0.wireOp",EDGE,"E42.filletArc"),sQuery(id+"F0.wireOp",EDGE,"E43.filletArc"),sQuery(id+"F0.wireOp",EDGE,"E44.filletArc"),sQuery(id+"F0.wireOp",EDGE,"E45.top"),sQuery(id+"F0.wireOp",EDGE,"E45.left"),sQuery(id+"F0.wireOp",EDGE,"E45.right"),sQuery(id+"F0.wireOp",EDGE,"E46.trimOffspring"),sQuery(id+"F0.wireOp",EDGE,"E47.filletArc"),sQuery(id+"F0.wireOp",EDGE,"E48.filletArc"),sQuery(id+"F0.wireOp",EDGE,"E49.filletArc"),sQuery(id+"F0.wireOp",EDGE,"E50.filletArc"),sQuery(id+"F0.wireOp",EDGE,"E52.MirrorCS"),sQuery(id+"F0.wireOp",EDGE,"E53.MirrorCS"),sQuery(id+"F0.wireOp",EDGE,"E54.MirrorCS"),sQuery(id+"F0.wireOp",EDGE,"E55.MirrorCS"),sQuery(id+"F0.wireOp",EDGE,"E56.MirrorCS"),sQuery(id+"F0.wireOp",EDGE,"E57.MirrorCS"),sQuery(id+"F0.wireOp",EDGE,"E58.MirrorCS"),sQuery(id+"F0.wireOp",EDGE,"E59.MirrorCS"),sQuery(id+"F0.wireOp",EDGE,"E60.bottom"),sQuery(id+"F0.wireOp",EDGE,"E60.top"),sQuery(id+"F0.wireOp",EDGE,"E60.left"),sQuery(id+"F0.wireOp",EDGE,"E60.right"),sQuery(id+"F0.wireOp",EDGE,"E61.MirrorCS"),sQuery(id+"F0.wireOp",EDGE,"E62.MirrorCS"),sQuery(id+"F0.wireOp",EDGE,"E63.MirrorCS"),sQuery(id+"F0.wireOp",EDGE,"E64.MirrorCS"),sQuery(id+"F0.wireOp",EDGE,"E65.bottom"),sQuery(id+"F0.wireOp",EDGE,"E65.top"),sQuery(id+"F0.wireOp",EDGE,"E65.left"),sQuery(id+"F0.wireOp",EDGE,"E65.right"),sQuery(id+"F0.wireOp",EDGE,"E66.MirrorCS"),sQuery(id+"F0.wireOp",EDGE,"E67.MirrorCS"),sQuery(id+"F0.wireOp",EDGE,"E68.MirrorCS"),sQuery(id+"F0.wireOp",EDGE,"E69.MirrorCS"),sQuery(id+"F0.wireOp",EDGE,"E70.bottom"),sQuery(id+"F0.wireOp",EDGE,"E70.top"),sQuery(id+"F0.wireOp",EDGE,"E70.left"),sQuery(id+"F0.wireOp",EDGE,"E70.right"),sQuery(id+"F0.wireOp",EDGE,"E71.filletArc"),sQuery(id+"F0.wireOp",EDGE,"E72.filletArc"),sQuery(id+"F0.wireOp",EDGE,"E73.filletArc"),sQuery(id+"F0.wireOp",EDGE,"E74.filletArc"),sQuery(id+"F0.wireOp",EDGE,"E75.filletArc"),sQuery(id+"F0.wireOp",EDGE,"E76.filletArc"),sQuery(id+"F0.wireOp",EDGE,"E77.filletArc"),sQuery(id+"F0.wireOp",EDGE,"E78.filletArc"),sQuery(id+"F0.wireOp",EDGE,"E79.filletArc"),sQuery(id+"F0.wireOp",EDGE,"E80.filletArc"),sQuery(id+"F0.wireOp",EDGE,"E81.filletArc"),sQuery(id+"F0.wireOp",EDGE,"E82.filletArc"),sQuery(id+"F0.wireOp",EDGE,"E83.filletArc"),sQuery(id+"F0.wireOp",EDGE,"E84.filletArc"),sQuery(id+"F0.wireOp",EDGE,"E85.filletArc"),sQuery(id+"F0.wireOp",EDGE,"E86.filletArc"),sQuery(id+"F0.wireOp",EDGE,"E87.filletArc"),sQuery(id+"F0.wireOp",EDGE,"E88.filletArc"),sQuery(id+"F0.wireOp",EDGE,"E89.filletArc"),sQuery(id+"F0.wireOp",EDGE,"E90.filletArc"),sQuery(id+"F0.wireOp",EDGE,"E91.bottom"),sQuery(id+"F0.wireOp",EDGE,"E91.top"),sQuery(id+"F0.wireOp",EDGE,"E91.left"),sQuery(id+"F0.wireOp",EDGE,"E91.right"),sQuery(id+"F0.wireOp",EDGE,"E92.MirrorCS"),sQuery(id+"F0.wireOp",EDGE,"E93.MirrorCS"),sQuery(id+"F0.wireOp",EDGE,"E94.MirrorCS"),sQuery(id+"F0.wireOp",EDGE,"E95.MirrorCS"),sQuery(id+"F0.wireOp",EDGE,"E96.bottom"),sQuery(id+"F0.wireOp",EDGE,"E96.top"),sQuery(id+"F0.wireOp",EDGE,"E96.left"),sQuery(id+"F0.wireOp",EDGE,"E96.right"),sQuery(id+"F0.wireOp",EDGE,"E97.bottom"),sQuery(id+"F0.wireOp",EDGE,"E97.top"),sQuery(id+"F0.wireOp",EDGE,"E97.left"),sQuery(id+"F0.wireOp",EDGE,"E97.right")])],"isStart":false});
            var sketch = newSketch(context, id + "F3", { "sketchPlane" : qUnion([Q0])});
            skLineSegment(sketch, "E134.bottom", {"start": v(-22.5, 73.26) * mm, "end": v(-21, 73.26) * mm});
            skLineSegment(sketch, "E134.top", {"start": v(-22.5, -62.27) * mm, "end": v(-21, -62.27) * mm});
            skLineSegment(sketch, "E134.left", {"start": v(-22.5, 73.26) * mm, "end": v(-22.5, -62.27) * mm});
            skLineSegment(sketch, "E134.right", {"start": v(-21, 73.26) * mm, "end": v(-21, -62.27) * mm});
            skLineSegment(sketch, "E135.MirrorCS", {"start": v(22.5, 73.26) * mm, "end": v(21, 73.26) * mm});
            skLineSegment(sketch, "E136.MirrorCS", {"start": v(22.5, -62.27) * mm, "end": v(21, -62.27) * mm});
            skLineSegment(sketch, "E137.MirrorCS", {"start": v(21, 73.26) * mm, "end": v(21, -62.27) * mm});
            skLineSegment(sketch, "E138.MirrorCS", {"start": v(22.5, 73.26) * mm, "end": v(22.5, -62.27) * mm});
            skLineSegment(sketch, "E139.bottom", {"start": v(-15, 97.73) * mm, "end": v(-13.5, 97.73) * mm});
            skLineSegment(sketch, "E139.top", {"start": v(-15, 85.73) * mm, "end": v(-13.5, 85.73) * mm});
            skLineSegment(sketch, "E139.left", {"start": v(-15, 97.73) * mm, "end": v(-15, 85.73) * mm});
            skLineSegment(sketch, "E139.right", {"start": v(-13.5, 97.73) * mm, "end": v(-13.5, 85.73) * mm});
            skLineSegment(sketch, "E140.bottom", {"start": v(-0.5, 97.73) * mm, "end": v(1, 97.73) * mm});
            skLineSegment(sketch, "E140.top", {"start": v(-0.5, 85.73) * mm, "end": v(1, 85.73) * mm});
            skLineSegment(sketch, "E140.left", {"start": v(-0.5, 97.73) * mm, "end": v(-0.5, 85.73) * mm});
            skLineSegment(sketch, "E140.right", {"start": v(1, 97.73) * mm, "end": v(1, 85.73) * mm});
            skSolve(sketch);
        }
        {
            var Q0;
            Q0 = qSketchRegion(id + "F3", true);
            extrude(context, id + "F4", {"entities" : qUnion([Q0]), "operationType" : NewBodyOperationType.ADD, "depth" : 1.5 * mm, "offsetDistance" : 25 * mm});
        }
        {
            var Q0;
            Q0=makeQuery(id+"F4.opExtrude","CAP_FACE",FACE,{"disambiguationData":[OSD([sQuery(id+"F3.wireOp",EDGE,"E135.MirrorCS"),sQuery(id+"F3.wireOp",EDGE,"E136.MirrorCS"),sQuery(id+"F3.wireOp",EDGE,"E137.MirrorCS"),sQuery(id+"F3.wireOp",EDGE,"E138.MirrorCS")])],"isStart":true});
            var sketch = newSketch(context, id + "F5", { "sketchPlane" : qUnion([Q0])});
            skLineSegment(sketch, "E141.0.0", {"start": v(-22.5, 37.33) * mm, "end": v(-22.5, 34.13) * mm});
            skArc(sketch, "E141.0.1", {"start": v(-22.5, 34.13) * mm, "mid": v(-21.59, 34.42) * mm, "end": v(-21, 35.17) * mm});
            skLineSegment(sketch, "E141.0.2", {"start": v(-21, 35.17) * mm, "end": v(-21, 36.29) * mm});
            skArc(sketch, "E141.0.3", {"start": v(-21, 36.29) * mm, "mid": v(-21.59, 37.04) * mm, "end": v(-22.5, 37.33) * mm});
            skArc(sketch, "E142.0.0", {"start": v(21, 35.17) * mm, "mid": v(21.59, 34.42) * mm, "end": v(22.5, 34.13) * mm});
            skLineSegment(sketch, "E142.0.1", {"start": v(22.5, 34.13) * mm, "end": v(22.5, 37.33) * mm});
            skArc(sketch, "E142.0.2", {"start": v(22.5, 37.33) * mm, "mid": v(21.59, 37.04) * mm, "end": v(21, 36.29) * mm});
            skLineSegment(sketch, "E142.0.3", {"start": v(21, 36.29) * mm, "end": v(21, 35.17) * mm});
            skSolve(sketch);
        }
        {
            var Q0;
            Q0 = qSketchRegion(id + "F5", true);
            extrude(context, id + "F6", {"entities" : qUnion([Q0]), "operationType" : NewBodyOperationType.REMOVE, "oppositeDirection" : true, "depth" : 25 * mm, "offsetDistance" : 25 * mm});
        }
        {
            var Q0;
            {var subQ0=sQuery(id+"F0.wireOp",EDGE,"E83.filletArc");var subQ1=sQuery(id+"F0.wireOp",EDGE,"E82.filletArc");var subQ2=sQuery(id+"F0.wireOp",EDGE,"E81.filletArc");var subQ3=sQuery(id+"F0.wireOp",EDGE,"E80.filletArc");var subQ4=sQuery(id+"F0.wireOp",EDGE,"E79.filletArc");var subQ5=sQuery(id+"F0.wireOp",EDGE,"E78.filletArc");var subQ6=sQuery(id+"F0.wireOp",EDGE,"E77.filletArc");var subQ7=sQuery(id+"F0.wireOp",EDGE,"E76.filletArc");var subQ8=sQuery(id+"F0.wireOp",EDGE,"E75.filletArc");var subQ9=sQuery(id+"F0.wireOp",EDGE,"E74.filletArc");var subQ10=sQuery(id+"F0.wireOp",EDGE,"E73.filletArc");var subQ11=sQuery(id+"F0.wireOp",EDGE,"E72.filletArc");var subQ12=sQuery(id+"F0.wireOp",EDGE,"E71.filletArc");var subQ13=sQuery(id+"F0.wireOp",EDGE,"E70.right");var subQ14=sQuery(id+"F0.wireOp",EDGE,"E70.left");var subQ15=sQuery(id+"F0.wireOp",EDGE,"E70.top");var subQ16=sQuery(id+"F0.wireOp",EDGE,"E70.bottom");var subQ17=sQuery(id+"F0.wireOp",EDGE,"E69.MirrorCS");var subQ18=sQuery(id+"F0.wireOp",EDGE,"E68.MirrorCS");var subQ19=sQuery(id+"F0.wireOp",EDGE,"E67.MirrorCS");var subQ20=sQuery(id+"F0.wireOp",EDGE,"E66.MirrorCS");var subQ21=sQuery(id+"F0.wireOp",EDGE,"E65.right");var subQ22=sQuery(id+"F0.wireOp",EDGE,"E65.left");var subQ23=sQuery(id+"F0.wireOp",EDGE,"E65.top");var subQ24=sQuery(id+"F0.wireOp",EDGE,"E65.bottom");var subQ25=sQuery(id+"F0.wireOp",EDGE,"E64.MirrorCS");var subQ26=sQuery(id+"F0.wireOp",EDGE,"E63.MirrorCS");var subQ27=sQuery(id+"F0.wireOp",EDGE,"E62.MirrorCS");var subQ28=sQuery(id+"F0.wireOp",EDGE,"E61.MirrorCS");var subQ29=sQuery(id+"F0.wireOp",EDGE,"E60.right");var subQ30=sQuery(id+"F0.wireOp",EDGE,"E60.left");var subQ31=sQuery(id+"F0.wireOp",EDGE,"E60.top");var subQ32=sQuery(id+"F0.wireOp",EDGE,"E60.bottom");var subQ33=sQuery(id+"F0.wireOp",EDGE,"E59.MirrorCS");var subQ34=sQuery(id+"F0.wireOp",EDGE,"E58.MirrorCS");var subQ35=sQuery(id+"F0.wireOp",EDGE,"E57.MirrorCS");var subQ36=sQuery(id+"F0.wireOp",EDGE,"E56.MirrorCS");var subQ37=sQuery(id+"F0.wireOp",EDGE,"E55.MirrorCS");var subQ38=sQuery(id+"F0.wireOp",EDGE,"E54.MirrorCS");var subQ39=sQuery(id+"F0.wireOp",EDGE,"E53.MirrorCS");var subQ40=sQuery(id+"F0.wireOp",EDGE,"E52.MirrorCS");var subQ41=sQuery(id+"F0.wireOp",EDGE,"E48.filletArc");var subQ42=sQuery(id+"F0.wireOp",EDGE,"E47.filletArc");var subQ43=sQuery(id+"F0.wireOp",EDGE,"E46.trimOffspring");var subQ44=sQuery(id+"F0.wireOp",EDGE,"E45.right");var subQ45=sQuery(id+"F0.wireOp",EDGE,"E45.left");var subQ46=sQuery(id+"F0.wireOp",EDGE,"E44.filletArc");var subQ47=sQuery(id+"F0.wireOp",EDGE,"E43.filletArc");var subQ48=sQuery(id+"F0.wireOp",EDGE,"E42.filletArc");var subQ49=sQuery(id+"F0.wireOp",EDGE,"E19.MirrorCS");var subQ50=sQuery(id+"F0.wireOp",EDGE,"E18.MirrorCS");var subQ51=sQuery(id+"F0.wireOp",EDGE,"E17.MirrorCS");var subQ52=sQuery(id+"F0.wireOp",EDGE,"E16.MirrorCS");var subQ53=sQuery(id+"F0.wireOp",EDGE,"E15.right");var subQ54=sQuery(id+"F0.wireOp",EDGE,"E15.left");var subQ55=sQuery(id+"F0.wireOp",EDGE,"E15.top");var subQ56=sQuery(id+"F0.wireOp",EDGE,"E15.bottom");var subQ57=sQuery(id+"F0.wireOp",EDGE,"E14.filletArc");var subQ58=sQuery(id+"F0.wireOp",EDGE,"E13.filletArc");var subQ59=sQuery(id+"F0.wireOp",EDGE,"E12.trimOffspring");var subQ60=sQuery(id+"F0.wireOp",EDGE,"E6.right");var subQ61=sQuery(id+"F0.wireOp",EDGE,"E6.left");var subQ62=sQuery(id+"F0.wireOp",EDGE,"E7.top");var subQ63=sQuery(id+"F0.wireOp",EDGE,"E20");var subQ64=sQuery(id+"F0.wireOp",EDGE,"E84.filletArc");var subQ65=sQuery(id+"F0.wireOp",EDGE,"E6.top");var subQ66=sQuery(id+"F0.wireOp",EDGE,"E41.filletArc");var subQ67=sQuery(id+"F0.wireOp",EDGE,"E11.filletArc");var subQ68=sQuery(id+"F0.wireOp",EDGE,"E7.left");var subQ69=sQuery(id+"F0.wireOp",EDGE,"E7.right");var subQ70=sQuery(id+"F0.wireOp",EDGE,"E8.filletArc");var subQ71=sQuery(id+"F0.wireOp",EDGE,"E9.filletArc");var subQ72=sQuery(id+"F0.wireOp",EDGE,"E10.filletArc");var subQ73=sQuery(id+"F0.wireOp",EDGE,"E21");var subQ74=sQuery(id+"F0.wireOp",EDGE,"E22");var subQ75=sQuery(id+"F0.wireOp",EDGE,"E23.top");var subQ76=sQuery(id+"F0.wireOp",EDGE,"E23.left");var subQ77=sQuery(id+"F0.wireOp",EDGE,"E23.right");var subQ78=sQuery(id+"F0.wireOp",EDGE,"E24.bottom");var subQ79=sQuery(id+"F0.wireOp",EDGE,"E24.top");var subQ80=sQuery(id+"F0.wireOp",EDGE,"E24.left");var subQ81=sQuery(id+"F0.wireOp",EDGE,"E24.right");var subQ82=sQuery(id+"F0.wireOp",EDGE,"E26.MirrorCS");var subQ83=sQuery(id+"F0.wireOp",EDGE,"E27.MirrorCS");var subQ84=sQuery(id+"F0.wireOp",EDGE,"E28.MirrorCS");var subQ85=sQuery(id+"F0.wireOp",EDGE,"E29.MirrorCS");var subQ86=sQuery(id+"F0.wireOp",EDGE,"E31.MirrorCS");var subQ87=sQuery(id+"F0.wireOp",EDGE,"E32.MirrorCS");var subQ88=sQuery(id+"F0.wireOp",EDGE,"E33.MirrorCS");var subQ89=sQuery(id+"F0.wireOp",EDGE,"E34.MirrorCS");var subQ90=sQuery(id+"F0.wireOp",EDGE,"E35.MirrorCS");var subQ91=sQuery(id+"F0.wireOp",EDGE,"E36.MirrorCS");var subQ92=sQuery(id+"F0.wireOp",EDGE,"E37.MirrorCS");var subQ93=sQuery(id+"F0.wireOp",EDGE,"E38.MirrorCS");var subQ94=sQuery(id+"F0.wireOp",EDGE,"E39.filletArc");var subQ95=sQuery(id+"F0.wireOp",EDGE,"E40.filletArc");var subQ96=sQuery(id+"F0.wireOp",EDGE,"E85.filletArc");var subQ98=sQuery(id+"F0.wireOp",EDGE,"E86.filletArc");var subQ102=sQuery(id+"F0.wireOp",EDGE,"E87.filletArc");var subQ103=sQuery(id+"F0.wireOp",EDGE,"E88.filletArc");var subQ104=sQuery(id+"F0.wireOp",EDGE,"E89.filletArc");var subQ106=sQuery(id+"F0.wireOp",EDGE,"E114.filletArc");var subQ108=sQuery(id+"F0.wireOp",EDGE,"E108");var subQ109=sQuery(id+"F0.wireOp",EDGE,"E106");var subQ112=sQuery(id+"F0.wireOp",EDGE,"E107");var subQ114=sQuery(id+"F0.wireOp",EDGE,"E113.filletArc");var subQ116=sQuery(id+"F0.wireOp",EDGE,"E90.filletArc");var subQ117=sQuery(id+"F0.wireOp",EDGE,"E91.bottom");var subQ118=sQuery(id+"F0.wireOp",EDGE,"E91.top");var subQ120=sQuery(id+"F0.wireOp",EDGE,"E91.left");var subQ124=sQuery(id+"F0.wireOp",EDGE,"E91.right");var subQ125=sQuery(id+"F0.wireOp",EDGE,"E92.MirrorCS");var subQ126=sQuery(id+"F0.wireOp",EDGE,"E93.MirrorCS");var subQ127=sQuery(id+"F0.wireOp",EDGE,"E94.MirrorCS");var subQ129=sQuery(id+"F0.wireOp",EDGE,"E132.MirrorCS");var subQ131=sQuery(id+"F0.wireOp",EDGE,"E130.MirrorCS");var subQ132=sQuery(id+"F0.wireOp",EDGE,"E128.MirrorCS");var subQ135=sQuery(id+"F0.wireOp",EDGE,"E129.MirrorCS");var subQ137=sQuery(id+"F0.wireOp",EDGE,"E131.MirrorCS");var subQ139=sQuery(id+"F0.wireOp",EDGE,"E95.MirrorCS");var subQ140=sQuery(id+"F0.wireOp",EDGE,"E96.bottom");var subQ141=sQuery(id+"F0.wireOp",EDGE,"E96.top");var subQ142=sQuery(id+"F0.wireOp",EDGE,"E96.left");var subQ143=sQuery(id+"F0.wireOp",EDGE,"E96.right");var subQ144=sQuery(id+"F0.wireOp",EDGE,"E97.bottom");var subQ145=sQuery(id+"F0.wireOp",EDGE,"E97.top");var subQ146=sQuery(id+"F0.wireOp",EDGE,"E97.left");var subQ147=sQuery(id+"F0.wireOp",EDGE,"E97.right");var subQ148=sQuery(id+"F0.wireOp",EDGE,"E98.bottom");var subQ149=sQuery(id+"F0.wireOp",EDGE,"E98.left");var subQ150=sQuery(id+"F0.wireOp",EDGE,"E98.right");var subQ151=sQuery(id+"F0.wireOp",EDGE,"E101.filletArc");var subQ152=sQuery(id+"F0.wireOp",EDGE,"E102.filletArc");var subQ153=sQuery(id+"F0.wireOp",EDGE,"E103.filletArc");var subQ154=sQuery(id+"F0.wireOp",EDGE,"E104.filletArc");var subQ155=sQuery(id+"F0.wireOp",EDGE,"E112.trimOffspring");var subQ156=sQuery(id+"F0.wireOp",EDGE,"E115.bottom");var subQ157=sQuery(id+"F0.wireOp",EDGE,"E115.top");var subQ158=sQuery(id+"F0.wireOp",EDGE,"E115.left");var subQ159=sQuery(id+"F0.wireOp",EDGE,"E115.right");var subQ160=sQuery(id+"F0.wireOp",EDGE,"E116.MirrorCS");var subQ161=sQuery(id+"F0.wireOp",EDGE,"E117.MirrorCS");var subQ162=sQuery(id+"F0.wireOp",EDGE,"E118.MirrorCS");var subQ163=sQuery(id+"F0.wireOp",EDGE,"E119.MirrorCS");var subQ164=sQuery(id+"F0.wireOp",EDGE,"E133.trimOffspring");Q0=makeQuery(id+"F4.boolean.opBoolean","SPLIT",FACE,{"disambiguationData":[TD([makeQuery(id+"F1.opExtrude","SWEPT_FACE",FACE,{"disambiguationData":[OSD([subQ65])]})])],"derivedFrom":makeQuery(id+"F1.opExtrude","CAP_FACE",FACE,{"disambiguationData":[OSD([subQ65,subQ61,subQ60,subQ62,subQ68,subQ69,subQ70,subQ71,subQ72,subQ67,subQ59,subQ58,subQ57,subQ56,subQ55,subQ54,subQ53,subQ52,subQ51,subQ50,subQ49,subQ63,subQ73,subQ74,subQ75,subQ76,subQ77,subQ78,subQ79,subQ80,subQ81,subQ82,subQ83,subQ84,subQ85,subQ86,subQ87,subQ88,subQ89,subQ90,subQ91,subQ92,subQ93,subQ94,subQ95,subQ66,subQ48,subQ47,subQ46,subQ45,subQ44,subQ43,subQ42,subQ41,subQ40,subQ39,subQ38,subQ37,subQ36,subQ35,subQ34,subQ33,subQ32,subQ31,subQ30,subQ29,subQ28,subQ27,subQ26,subQ25,subQ24,subQ23,subQ22,subQ21,subQ20,subQ19,subQ18,subQ17,subQ16,subQ15,subQ14,subQ13,subQ12,subQ11,subQ10,subQ9,subQ8,subQ7,subQ6,subQ5,subQ4,subQ3,subQ2,subQ1,subQ0,subQ64,subQ96,subQ98,subQ102,subQ103,subQ104,subQ116,subQ117,subQ118,subQ120,subQ124,subQ125,subQ126,subQ127,subQ139,subQ140,subQ141,subQ142,subQ143,subQ144,subQ145,subQ146,subQ147,subQ148,subQ149,subQ150,subQ151,subQ152,subQ153,subQ154,sQuery(id+"F0.wireOp",EDGE,"E105"),subQ109,subQ112,subQ108,sQuery(id+"F0.wireOp",EDGE,"E109.trimOffspring"),sQuery(id+"F0.wireOp",EDGE,"E110.filletArc"),sQuery(id+"F0.wireOp",EDGE,"E111.filletArc"),subQ155,subQ114,subQ106,subQ156,subQ157,subQ158,subQ159,subQ160,subQ161,subQ162,subQ163,sQuery(id+"F0.wireOp",EDGE,"E120.MirrorCS"),sQuery(id+"F0.wireOp",EDGE,"E123.MirrorCS"),sQuery(id+"F0.wireOp",EDGE,"E125.MirrorCS"),sQuery(id+"F0.wireOp",EDGE,"E127.MirrorCS"),subQ132,subQ135,subQ131,subQ137,subQ129,subQ164])],"isStart":false})});}
            var sketch = newSketch(context, id + "F7", { "sketchPlane" : qUnion([Q0])});
            skCircle(sketch, "E143.0", {"center": v(-17, 70.73) * mm, "radius": 1.6 * mm, "construction": true});
            skCircle(sketch, "E144.0", {"center": v(17, 70.73) * mm, "radius": 1.6 * mm, "construction": true});
            skLineSegment(sketch, "E145", {"start": v(0, 5.73) * mm, "end": v(20, 5.73) * mm});
            skLineSegment(sketch, "E146", {"start": v(21, 5.73) * mm, "end": v(21, 33.98) * mm});
            skLineSegment(sketch, "E147", {"start": v(20, 19.23) * mm, "end": v(12.5, 19.23) * mm});
            skLineSegment(sketch, "E148", {"start": v(12.5, 19.23) * mm, "end": v(12.5, 32.93) * mm});
            skLineSegment(sketch, "E149", {"start": v(12.5, 32.93) * mm, "end": v(16.5, 32.93) * mm});
            skLineSegment(sketch, "E150", {"start": v(16.5, 40.96) * mm, "end": v(20, 40.96) * mm});
            skLineSegment(sketch, "E151", {"start": v(21, 40.96) * mm, "end": v(21, 73.26) * mm});
            skLineSegment(sketch, "E152", {"start": v(14.47, 73.26) * mm, "end": v(0, 73.26) * mm});
            skLineSegment(sketch, "E153", {"start": v(0, 0) * mm, "end": v(0, 0) * mm});
            skLineSegment(sketch, "E154.0", {"start": v(20, 5.73) * mm, "end": v(20, 19.23) * mm});
            skLineSegment(sketch, "E155.0", {"start": v(16.5, 32.93) * mm, "end": v(16.5, 40.96) * mm});
            skPoint(sketch, "E156.start.orphan", {"position": v(17.5, 32.93) * mm});
            skLineSegment(sketch, "E157.0", {"start": v(20, 40.96) * mm, "end": v(20, 68.2) * mm});
            skPoint(sketch, "E158.orphan", {"position": v(21, 19.23) * mm});
            skLineSegment(sketch, "E159.MirrorCS", {"start": v(-14.47, 73.26) * mm, "end": v(0, 73.26) * mm});
            skLineSegment(sketch, "E160.MirrorCS", {"start": v(-20, 40.96) * mm, "end": v(-20, 68.2) * mm});
            skLineSegment(sketch, "E161.MirrorCS", {"start": v(-16.5, 40.96) * mm, "end": v(-20, 40.96) * mm});
            skLineSegment(sketch, "E162.MirrorCS", {"start": v(-16.5, 32.93) * mm, "end": v(-16.5, 40.96) * mm});
            skLineSegment(sketch, "E163.MirrorCS", {"start": v(-12.5, 32.93) * mm, "end": v(-16.5, 32.93) * mm});
            skLineSegment(sketch, "E164.MirrorCS", {"start": v(-12.5, 19.23) * mm, "end": v(-12.5, 32.93) * mm});
            skLineSegment(sketch, "E165.MirrorCS", {"start": v(-20, 19.23) * mm, "end": v(-12.5, 19.23) * mm});
            skLineSegment(sketch, "E166.MirrorCS", {"start": v(-20, 5.73) * mm, "end": v(-20, 19.23) * mm});
            skLineSegment(sketch, "E167.MirrorCS", {"start": v(-10, 5.73) * mm, "end": v(-20, 5.73) * mm});
            skArc(sketch, "E168", {"start": v(-17, 68.2) * mm, "mid": v(-15.21, 68.94) * mm, "end": v(-14.47, 70.73) * mm});
            skLineSegment(sketch, "E169", {"start": v(-17, 68.2) * mm, "end": v(-20, 68.2) * mm});
            skLineSegment(sketch, "E170", {"start": v(-14.47, 70.73) * mm, "end": v(-14.47, 73.26) * mm});
            skPoint(sketch, "E171.orphan", {"position": v(-20, 73.26) * mm});
            skLineSegment(sketch, "E172.MirrorCS", {"start": v(14.47, 70.73) * mm, "end": v(14.47, 73.26) * mm});
            skArc(sketch, "E173.MirrorCS", {"start": v(17, 68.2) * mm, "mid": v(15.21, 68.94) * mm, "end": v(14.47, 70.73) * mm});
            skLineSegment(sketch, "E174.MirrorCS", {"start": v(17, 68.2) * mm, "end": v(20, 68.2) * mm});
            skPoint(sketch, "E175.orphan", {"position": v(20, 73.26) * mm});
            skLineSegment(sketch, "E176.bottom", {"start": v(-10, 5.73) * mm, "end": v(0, 5.73) * mm});
            skLineSegment(sketch, "E176.top", {"start": v(-10, -8.26) * mm, "end": v(10, -8.26) * mm});
            skLineSegment(sketch, "E176.left", {"start": v(-10, 5.73) * mm, "end": v(-10, -8.26) * mm});
            skLineSegment(sketch, "E176.right", {"start": v(10, 5.73) * mm, "end": v(10, -8.26) * mm});
            skPoint(sketch, "E177.orphan", {"position": v(0, 5.73) * mm});
            skSolve(sketch);
        }
        {
            var Q0;
            Q0 = qSketchRegion(id + "F7", true);
            extrude(context, id + "F8", {"entities" : qUnion([Q0]), "depth" : 3 * mm, "offsetDistance" : 25 * mm});
        }
        {
            var Q0;
            Q0=makeQuery(id+"F8.opExtrude","CAP_FACE",FACE,{"disambiguationData":[OSD([sQuery(id+"F7.wireOp",EDGE,"E145"),sQuery(id+"F7.wireOp",EDGE,"E147"),sQuery(id+"F7.wireOp",EDGE,"E148"),sQuery(id+"F7.wireOp",EDGE,"E149"),sQuery(id+"F7.wireOp",EDGE,"E150"),sQuery(id+"F7.wireOp",EDGE,"E152"),sQuery(id+"F7.wireOp",EDGE,"E154.0"),sQuery(id+"F7.wireOp",EDGE,"E155.0"),sQuery(id+"F7.wireOp",EDGE,"E157.0"),sQuery(id+"F7.wireOp",EDGE,"E159.MirrorCS"),sQuery(id+"F7.wireOp",EDGE,"E160.MirrorCS"),sQuery(id+"F7.wireOp",EDGE,"E161.MirrorCS"),sQuery(id+"F7.wireOp",EDGE,"E162.MirrorCS"),sQuery(id+"F7.wireOp",EDGE,"E163.MirrorCS"),sQuery(id+"F7.wireOp",EDGE,"E164.MirrorCS"),sQuery(id+"F7.wireOp",EDGE,"E165.MirrorCS"),sQuery(id+"F7.wireOp",EDGE,"E166.MirrorCS"),sQuery(id+"F7.wireOp",EDGE,"E167.MirrorCS"),sQuery(id+"F7.wireOp",EDGE,"E168"),sQuery(id+"F7.wireOp",EDGE,"E169"),sQuery(id+"F7.wireOp",EDGE,"E170"),sQuery(id+"F7.wireOp",EDGE,"E172.MirrorCS"),sQuery(id+"F7.wireOp",EDGE,"E173.MirrorCS"),sQuery(id+"F7.wireOp",EDGE,"E174.MirrorCS"),sQuery(id+"F7.wireOp",EDGE,"E176.top"),sQuery(id+"F7.wireOp",EDGE,"E176.left"),sQuery(id+"F7.wireOp",EDGE,"E176.right")])],"isStart":true});
            var sketch = newSketch(context, id + "F9", { "sketchPlane" : qUnion([Q0])});
            skLineSegment(sketch, "E178.bottom", {"start": v(10, 3.73) * mm, "end": v(-10, 3.73) * mm});
            skLineSegment(sketch, "E178.top", {"start": v(10, 0) * mm, "end": v(-10, 0) * mm});
            skLineSegment(sketch, "E178.left", {"start": v(10, 3.73) * mm, "end": v(10, 0) * mm});
            skLineSegment(sketch, "E178.right", {"start": v(-10, 3.73) * mm, "end": v(-10, 0) * mm});
            skSolve(sketch);
        }
        {
            var Q0;
            Q0 = qSketchRegion(id + "F9", true);
            extrude(context, id + "F10", {"entities" : qUnion([Q0]), "operationType" : NewBodyOperationType.REMOVE, "oppositeDirection" : true, "depth" : 1.5 * mm, "offsetDistance" : 25 * mm});
        }
    });
